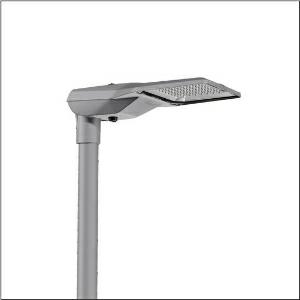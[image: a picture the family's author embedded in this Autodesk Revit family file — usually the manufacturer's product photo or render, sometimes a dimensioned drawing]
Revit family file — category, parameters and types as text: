
# Revit family: streetlight_sl_21_midi___st0_5a_5xe3b43t08lb_fa0c
name_source: partatom
category: Lighting Fixtures
units: mm (PartAtom-declared; Revit-internal decimal feet)

## family parameters
Cut with Voids When Loaded = No
Host = Face
Light Source = No
Part Type = Normal
Room Calculation Point = No
Round Connector Dimension = Use Diameter
Shared = No

## types (1)
- --- (1 x LED, 14950 lm, 99.6 W, 4000K)
    Apparent Load = 100 VA
    CIE Flux Codes = 41 75 97 100 100
    Color Rendering = 70
    Color Temperature = 4000K
    Default Elevation = 1800 mm
    Description = Streetlight SL 21 midi, mast luminaire, primary light control with lens, of PMMA, primary optical cover: cover, of toughened safety glass, transparent, light distribution: ST0.5a, light emission: direct distribution, primary light characteristic: asymmetric, installation type: side-entry, post-top, LED, High Power LED, rated luminous flux: 14.950lm, luminous efficacy: 150lm/W, light colour: 740, colour temperature: 4000K, control gear: D4i, control: overheat protection, constant luminous flux control, time-dependent luminous flux control, flexible luminous flux parameterisation, pre-setting: logarithmic dimming characteristic, mains connection: 230..240V, AC, 50/60Hz, start of lifetime: 100W, end of service life: 102W, reduction: 46W, luminaire housing, of diecast aluminium, powder-coated, SITECO metallic grey (DB 702S), corrosivity category C5 high according to DIN EN ISO 12944, please order mast flange separately, inclination adjustable: 0°, 5°, 10°, 15°, sealing non-destructively replaceable, multi-level sealing system, length: 644mm, width: 335mm, height: 110mm, mast flange for spigot size: 42mm (side-entry): 5XC10008XM4, 60/48mm (side-entry/post-top): 5XC10108XM2, 76/60mm (side-entry/post-top): 5XC10108XM1, mounting height: 4..8m, Smart Interface below and above, protection rating (complete): IP66, insulation class (complete): insulation class II (safety insulation), certification: CE, ENEC, ENEC+, VDE, impact resistance: IK10, permissible operating ambient temperature for outdoor applications: -40..+50°C, standard-compliant lighting for roads and squares, packaging unit: 1 piece

Light Distribution: ST0.5a
    Height = 111 mm
    Lamp = 1 x LED
    Lamp Light Flux = 14950 lm
    Lamp Power = 99.6 W
    Lamp count = 1
    Length = 644 mm
    Luminous efficacy = 150 lm/W
    Manufacturer = Siteco
    ModVariant = No
    Model = 5XE3B43T08LB
    Number of Poles = 1
    OnlyDefault = Yes
    Power Factor = 1
    Product Name = Streetlight SL 21 midi | ST0.5a
    Product group = mast luminaire | pylon top
    ProductGroupID = 6100
    Protection Class = Protection class II
    Protection Degree = IP 66
    RLX_Detail_Level = 1
    RLX_Emergency_Light_Flux = 0 lm
    RLX_Emergency_Type = 0
    RLX_Emergency_Type_DB = No
    RlxData = <blob elided: 37953 chars, md5=f86cd8a7>
    Socket = socket
    Standby Power = 0 W
    System Light Flux = 14950 lm
    System Power = 100 W
    Type Comments = factory setting: luminous flux: 100 % | dim-lin: 254 | 1020 mA
    Type Image = l_1004304.jpg
    URL = http://relux.com
    VarID = @adj_032299
    Voltage = 0 V
    Weight = 0.00 kg
    Width = 336 mm

## geometry (parser evidence)
native form markers: Blend x4, Sweep x9
no freeform markers — native parametric forms only
